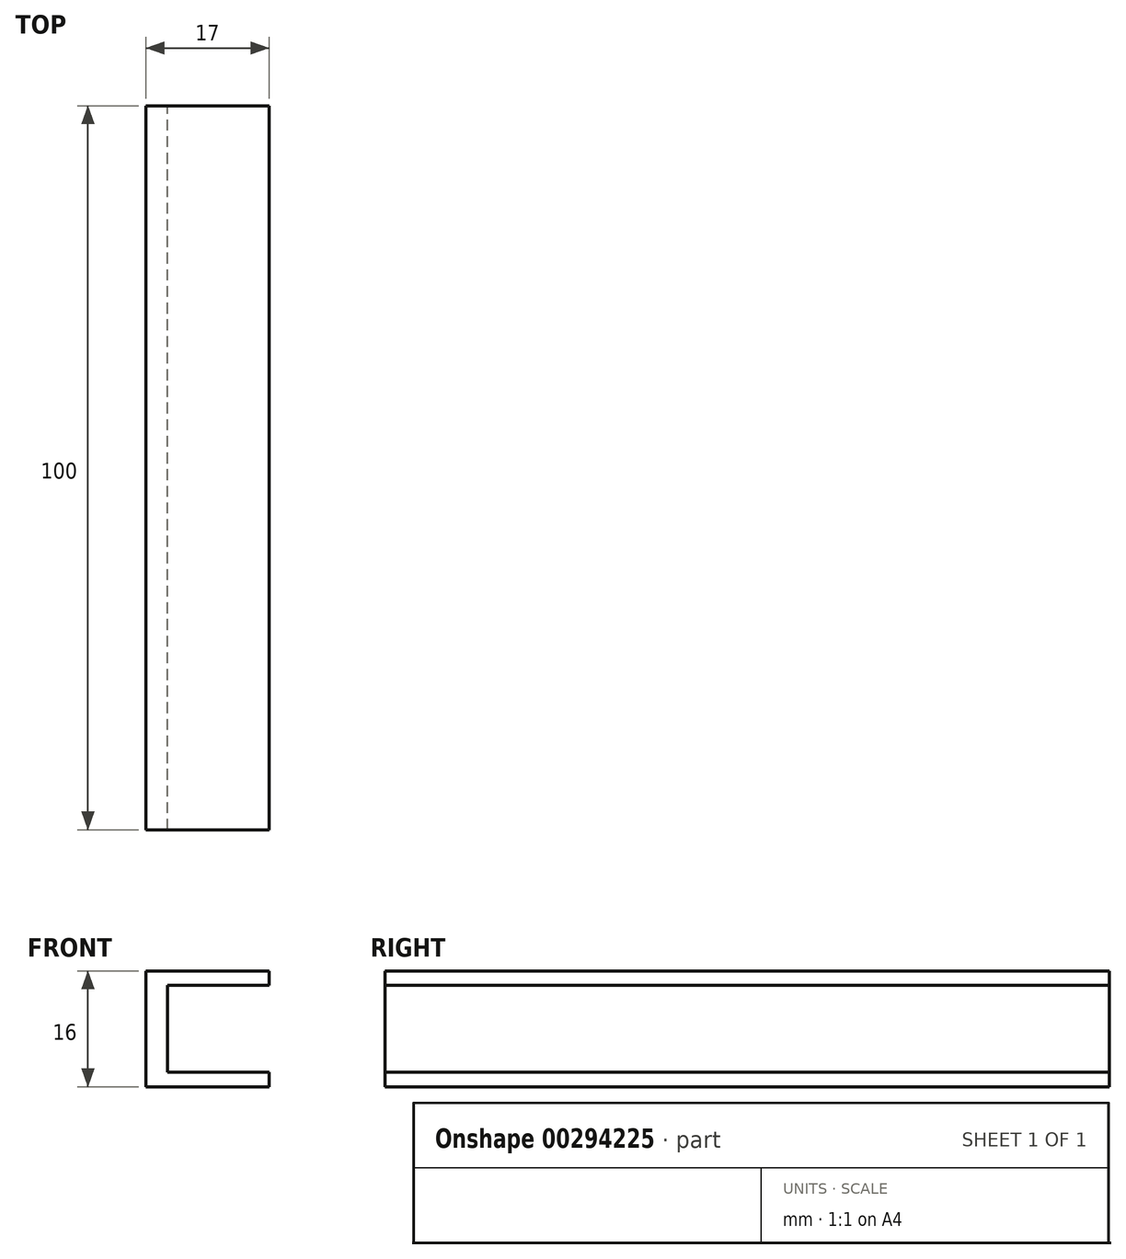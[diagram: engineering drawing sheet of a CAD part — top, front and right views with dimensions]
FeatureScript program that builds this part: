
annotation { "Feature Type Name" : "Feature", "Feature Type Description" : "" }
export const myFeature = defineFeature(function(context is Context, id is Id, definition is map)
    precondition{}
    {
        {
            var Q0;
            Q0=qCreatedBy(makeId("Front.planeOp"),FACE);
            var sketch = newSketch(context, id + "F0", { "sketchPlane" : qUnion([Q0])});
            skLineSegment(sketch, "E0.bottom", {"start": v(0, 0) * mm, "end": v(-17, 0) * mm});
            skLineSegment(sketch, "E0.top", {"start": v(0, 16) * mm, "end": v(-17, 16) * mm});
            skLineSegment(sketch, "E0.left", {"start": v(0, 0) * mm, "end": v(0, 2) * mm});
            skLineSegment(sketch, "E0.right", {"start": v(-17, 0) * mm, "end": v(-17, 16) * mm});
            skLineSegment(sketch, "E1.bottom", {"start": v(0, 14) * mm, "end": v(-14, 14) * mm});
            skLineSegment(sketch, "E2.trimOffspring", {"start": v(0, 14) * mm, "end": v(0, 16) * mm});
            skLineSegment(sketch, "E3", {"start": v(-14, 14) * mm, "end": v(-14, 2) * mm});
            skLineSegment(sketch, "E4", {"start": v(-14, 2) * mm, "end": v(0, 2) * mm});
            skSolve(sketch);
        }
        {
            var Q0;
            Q0 = qSketchRegion(id + "F0", true);
            extrude(context, id + "F1", {"entities" : qUnion([Q0]), "depth" : 100 * mm});
        }
    });
